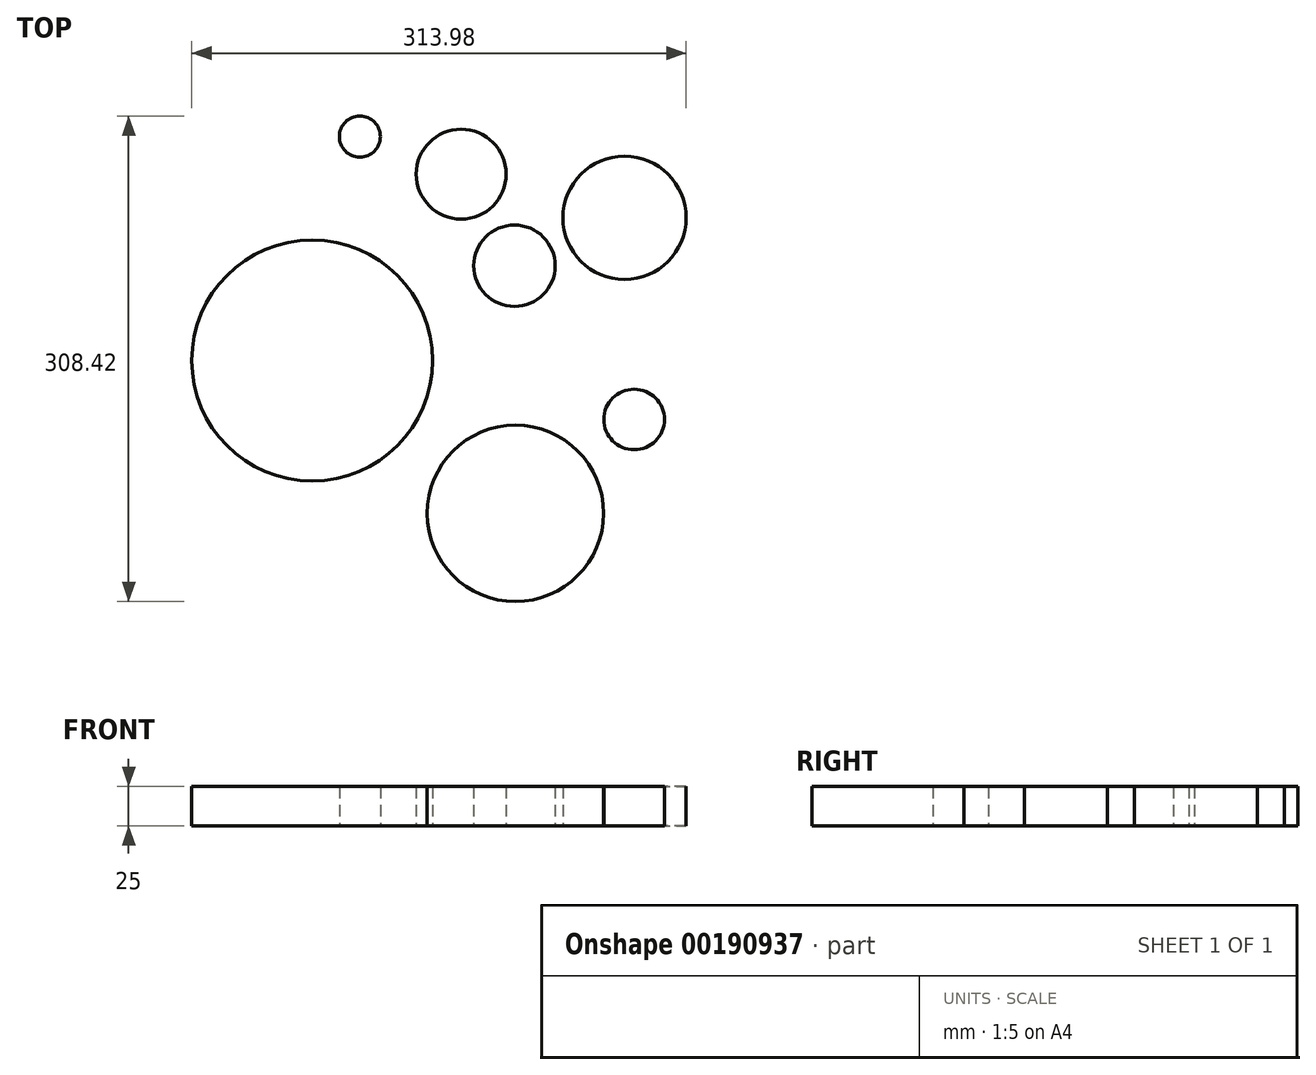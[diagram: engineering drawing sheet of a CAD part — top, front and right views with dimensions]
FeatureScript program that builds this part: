
annotation { "Feature Type Name" : "Feature", "Feature Type Description" : "" }
export const myFeature = defineFeature(function(context is Context, id is Id, definition is map)
    precondition{}
    {
        {
            var Q0;
            Q0=qCreatedBy(makeId("Top.planeOp"),FACE);
            var sketch = newSketch(context, id + "F0", { "sketchPlane" : qUnion([Q0])});
            skCircle(sketch, "E0", {"center": v(-79.14, 87.39) * mm, "radius": 13.03 * mm});
            skCircle(sketch, "E1", {"center": v(-14.77, 63.46) * mm, "radius": 28.53 * mm});
            skCircle(sketch, "E2", {"center": v(88.96, 35.74) * mm, "radius": 39.13 * mm});
            skCircle(sketch, "E3", {"center": v(19.07, 5.3) * mm, "radius": 25.86 * mm});
            skCircle(sketch, "E4", {"center": v(-109.4, -54.88) * mm, "radius": 76.5 * mm});
            skCircle(sketch, "E5", {"center": v(95.09, -92.32) * mm, "radius": 19.24 * mm});
            skCircle(sketch, "E6", {"center": v(19.66, -151.98) * mm, "radius": 56.02 * mm});
            skSolve(sketch);
        }
        {
            var Q0;
            Q0 = qSketchRegion(id + "F0", true);
            extrude(context, id + "F1", {"entities" : qUnion([Q0]), "depth" : 25 * mm});
        }
    });
